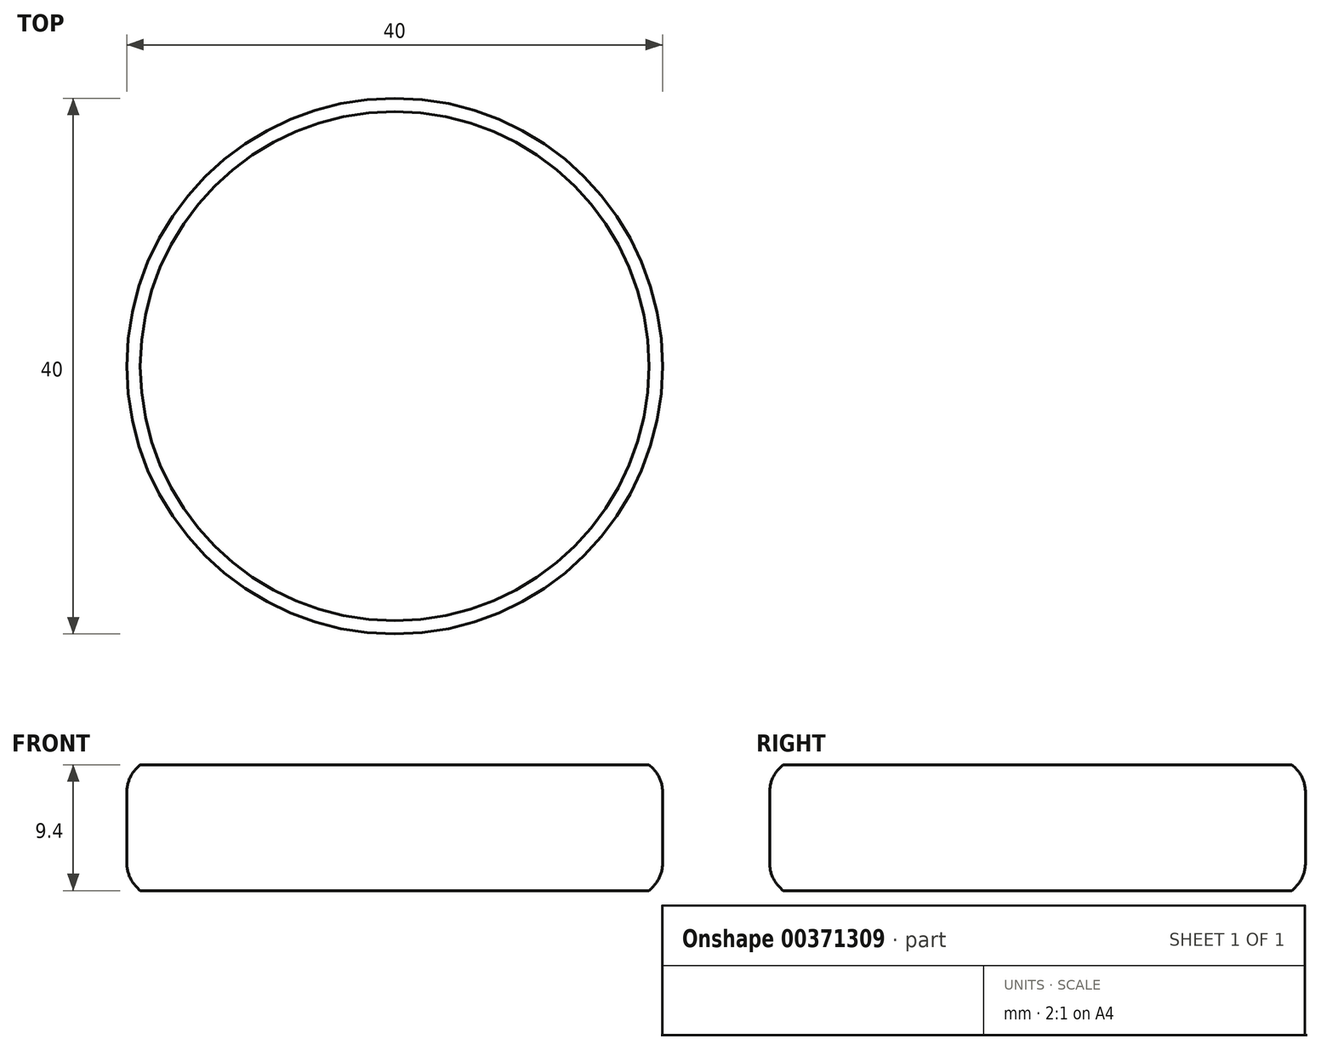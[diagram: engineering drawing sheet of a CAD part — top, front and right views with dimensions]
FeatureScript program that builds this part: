
annotation { "Feature Type Name" : "Feature", "Feature Type Description" : "" }
export const myFeature = defineFeature(function(context is Context, id is Id, definition is map)
    precondition{}
    {
        {
            var Q0;
            Q0=qCreatedBy(makeId("Top.planeOp"),FACE);
            var sketch = newSketch(context, id + "F0", { "sketchPlane" : qUnion([Q0])});
            skCircle(sketch, "E0", {"center": v(0, 0) * mm, "radius": 20 * mm});
            skSolve(sketch);
        }
        {
            var Q0;
            Q0 = qSketchRegion(id + "F0", true);
            extrude(context, id + "F1", {"entities" : qUnion([Q0]), "depth" : 9.4 * mm});
        }
        {
            var Q0;
            Q0=makeQuery(id+"F1.opExtrude","CAP_FACE",FACE,{"disambiguationData":[OSD([sQuery(id+"F0.wireOp",EDGE,"E0")])],"isStart":false});
            var Q1;
            Q1=makeQuery(id+"F1.opExtrude","CAP_FACE",FACE,{"disambiguationData":[OSD([sQuery(id+"F0.wireOp",EDGE,"E0")])],"isStart":true});
            chamfer(context, id + "F2", {"entities" : qUnion([Q0, Q1]), "width" : 1 * mm, "tangentPropagation" : true});
        }
        {
            var Q0;
            {var subQ0=sQuery(id+"F0.wireOp",EDGE,"E0");Q0=makeQuery(id+"F2.opChamfer","BLEND_EDGE",EDGE,{"blendedFrom":[makeQuery(id+"F1.opExtrude","CAP_EDGE",EDGE,{"disambiguationData":[OSD([subQ0])],"isStart":false}),makeQuery(id+"F1.opExtrude","SWEPT_FACE",FACE,{"disambiguationData":[OSD([subQ0])]})],"blendedInto":[makeQuery(id+"F1.opExtrude","SWEPT_FACE",FACE,{"disambiguationData":[OSD([subQ0])]})]});}
            var Q1;
            {var subQ0=sQuery(id+"F0.wireOp",EDGE,"E0");Q1=makeQuery(id+"F2.opChamfer","BLEND_EDGE",EDGE,{"blendedFrom":[makeQuery(id+"F1.opExtrude","CAP_EDGE",EDGE,{"disambiguationData":[OSD([subQ0])],"isStart":true}),makeQuery(id+"F1.opExtrude","SWEPT_FACE",FACE,{"disambiguationData":[OSD([subQ0])]})],"blendedInto":[makeQuery(id+"F1.opExtrude","SWEPT_FACE",FACE,{"disambiguationData":[OSD([subQ0])]})]});}
            fillet(context, id + "F3", {"entities" : qUnion([Q0, Q1]), "radius" : 2.5 * mm, "tangentPropagation" : true, "allowEdgeOverflow" : false});
        }
    });
